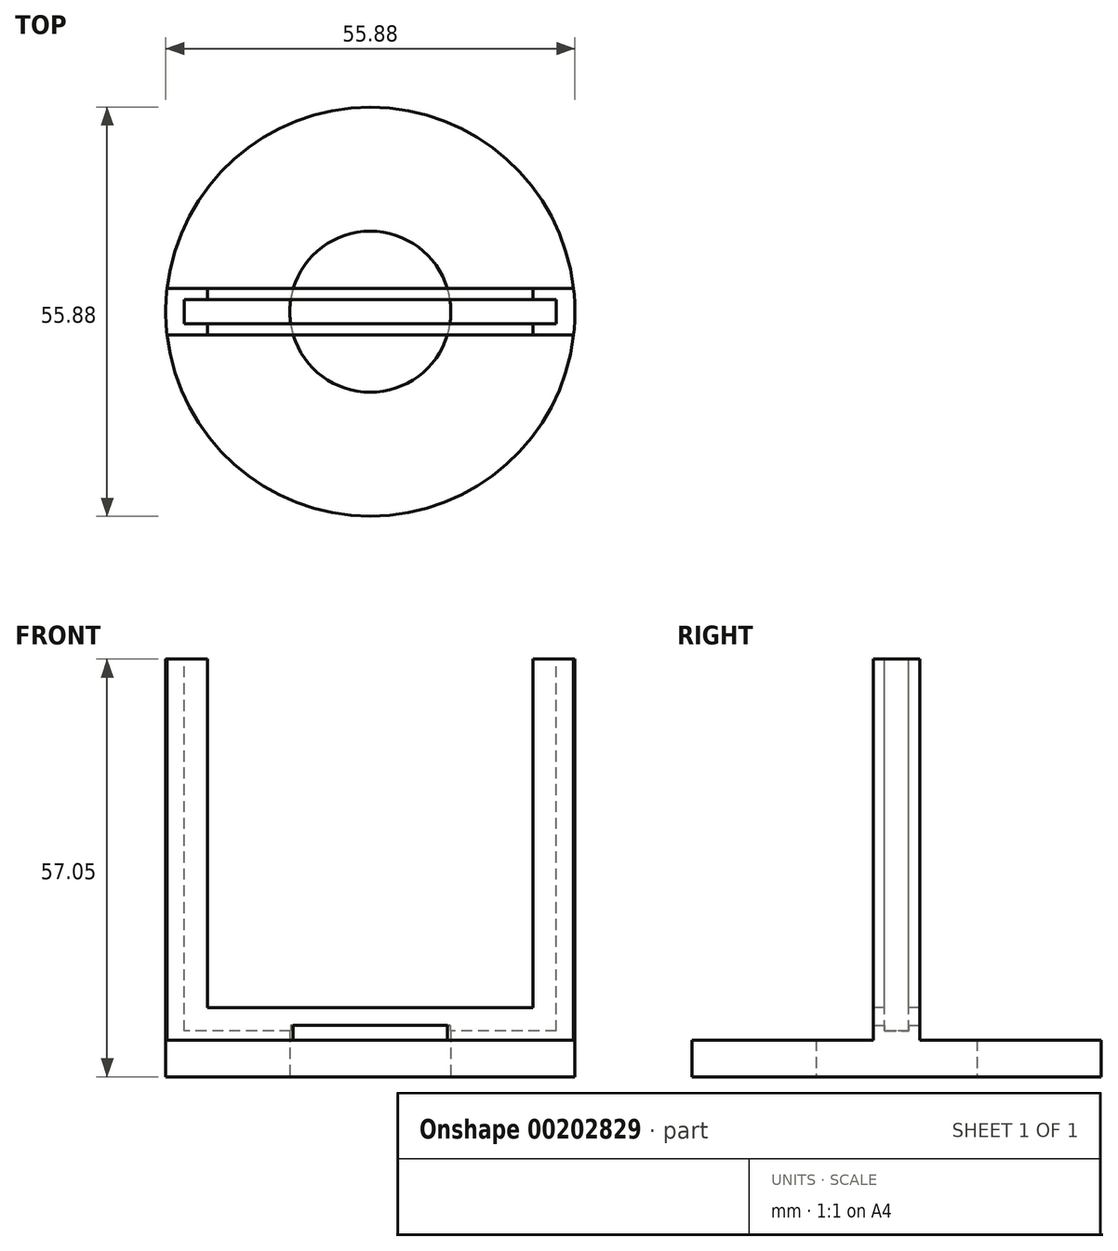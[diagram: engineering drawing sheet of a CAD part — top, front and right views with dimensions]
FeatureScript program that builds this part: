
annotation { "Feature Type Name" : "Feature", "Feature Type Description" : "" }
export const myFeature = defineFeature(function(context is Context, id is Id, definition is map)
    precondition{}
    {
        {
            var Q0;
            Q0=qCreatedBy(makeId("Top.planeOp"),FACE);
            var sketch = newSketch(context, id + "F0", { "sketchPlane" : qUnion([Q0])});
            skCircle(sketch, "E0", {"center": v(0, 0) * mm, "radius": 27.94 * mm});
            skSolve(sketch);
        }
        {
            var Q0;
            Q0=makeQuery(id+"F0.imprint","IMPRINT",FACE,{"disambiguationData":[TD([[makeQuery(id+"F0.imprint","IMPRINT",EDGE,{"derivedFrom":sQuery(id+"F0.wireOp",EDGE,"E0")}),1.0]])]});
            extrude(context, id + "F1", {"entities" : qUnion([Q0]), "depth" : 5 * mm});
        }
        {
            var Q0;
            Q0=makeQuery(id+"F1.opExtrude","CAP_FACE",FACE,{"disambiguationData":[OSD([sQuery(id+"F0.wireOp",EDGE,"E0")])],"isStart":false});
            var sketch = newSketch(context, id + "F2", { "sketchPlane" : qUnion([Q0])});
            skLineSegment(sketch, "E1.bottom", {"start": v(27.94, 3.18) * mm, "end": v(-27.94, 3.18) * mm});
            skLineSegment(sketch, "E1.top", {"start": v(27.94, -3.18) * mm, "end": v(-27.94, -3.18) * mm});
            skLineSegment(sketch, "E1.left", {"start": v(27.94, 3.18) * mm, "end": v(27.94, -3.18) * mm});
            skLineSegment(sketch, "E1.right", {"start": v(-27.94, 3.18) * mm, "end": v(-27.94, -3.18) * mm});
            skPoint(sketch, "E1.middle", {"position": v(0, 0) * mm});
            skSolve(sketch);
        }
        {
            var Q0;
            {var subQ0=sQuery(id+"F2.wireOp",EDGE,"E1.bottom");var subQ1=makeQuery(id+"F1.opExtrude","CAP_EDGE",EDGE,{"disambiguationData":[OSD([sQuery(id+"F0.wireOp",EDGE,"E0")])],"isStart":false});var subQ4=makeQuery(id+"F2.imprint","INTERSECT",VERTEX,{"disambiguationData":[OD(0.0)],"derivedFrom":[subQ1,subQ0]});Q0=makeQuery(id+"F2.imprint","IMPRINT",FACE,{"disambiguationData":[TD([[makeQuery(id+"F2.imprint","IMPRINT",EDGE,{"disambiguationData":[TD([[subQ4,-1.0]])],"derivedFrom":subQ0}),1.0]])]});}
            extrude(context, id + "F3", {"entities" : qUnion([Q0]), "operationType" : NewBodyOperationType.ADD, "depth" : 51.05 * mm + 1 * mm});
        }
        {
            var Q0;
            Q0=makeQuery(id+"F3.opExtrude","CAP_FACE",FACE,{"disambiguationData":[OSD([sQuery(id+"F0.wireOp",EDGE,"E0"),sQuery(id+"F2.wireOp",EDGE,"E1.bottom"),sQuery(id+"F2.wireOp",EDGE,"E1.top")])],"isStart":false});
            var sketch = newSketch(context, id + "F4", { "sketchPlane" : qUnion([Q0])});
            skLineSegment(sketch, "E2.bottom", {"start": v(25.4, 1.65) * mm, "end": v(-25.4, 1.65) * mm});
            skLineSegment(sketch, "E2.top", {"start": v(25.4, -1.65) * mm, "end": v(-25.4, -1.65) * mm});
            skLineSegment(sketch, "E2.left", {"start": v(25.4, 1.65) * mm, "end": v(25.4, -1.65) * mm});
            skLineSegment(sketch, "E2.right", {"start": v(-25.4, 1.65) * mm, "end": v(-25.4, -1.65) * mm});
            skPoint(sketch, "E2.middle", {"position": v(0, 0) * mm});
            skSolve(sketch);
        }
        {
            var Q0;
            Q0=makeQuery(id+"F4.imprint","IMPRINT",FACE,{"disambiguationData":[TD([[makeQuery(id+"F4.imprint","IMPRINT",EDGE,{"derivedFrom":sQuery(id+"F4.wireOp",EDGE,"E2.bottom")}),1.0]])]});
            extrude(context, id + "F5", {"entities" : qUnion([Q0]), "operationType" : NewBodyOperationType.REMOVE, "oppositeDirection" : true, "depth" : 50.8 * mm});
        }
        {
            var Q0;
            Q0=makeQuery(id+"F3.opExtrude","CAP_FACE",FACE,{"disambiguationData":[OSD([sQuery(id+"F0.wireOp",EDGE,"E0"),sQuery(id+"F2.wireOp",EDGE,"E1.bottom"),sQuery(id+"F2.wireOp",EDGE,"E1.top")])],"isStart":false});
            var sketch = newSketch(context, id + "F6", { "sketchPlane" : qUnion([Q0])});
            skLineSegment(sketch, "E3.bottom", {"start": v(22.23, 3.18) * mm, "end": v(-22.23, 3.18) * mm});
            skLineSegment(sketch, "E3.top", {"start": v(22.23, -3.18) * mm, "end": v(-22.23, -3.18) * mm});
            skLineSegment(sketch, "E3.left", {"start": v(22.23, 3.18) * mm, "end": v(22.23, -3.18) * mm});
            skLineSegment(sketch, "E3.right", {"start": v(-22.23, 3.18) * mm, "end": v(-22.23, -3.18) * mm});
            skPoint(sketch, "E3.middle", {"position": v(0, 0) * mm});
            skSolve(sketch);
        }
        {
            var Q0;
            Q0 = qSketchRegion(id + "F6", true);
            extrude(context, id + "F7", {"entities" : qUnion([Q0]), "operationType" : NewBodyOperationType.REMOVE, "oppositeDirection" : true, "depth" : 47.62 * mm});
        }
        {
            var Q0;
            Q0=makeQuery(id+"F1.opExtrude","CAP_FACE",FACE,{"disambiguationData":[OSD([sQuery(id+"F0.wireOp",EDGE,"E0")])],"isStart":true});
            var sketch = newSketch(context, id + "F8", { "sketchPlane" : qUnion([Q0])});
            skCircle(sketch, "E4", {"center": v(0, 0) * mm, "radius": 11 * mm});
            skSolve(sketch);
        }
        {
            var Q0;
            Q0=makeQuery(id+"F8.imprint","IMPRINT",FACE,{"disambiguationData":[TD([[makeQuery(id+"F8.imprint","IMPRINT",EDGE,{"derivedFrom":sQuery(id+"F8.wireOp",EDGE,"E4")}),1.0]])]});
            extrude(context, id + "F9", {"entities" : qUnion([Q0]), "operationType" : NewBodyOperationType.REMOVE, "oppositeDirection" : true, "depth" : 7 * mm});
        }
    });
